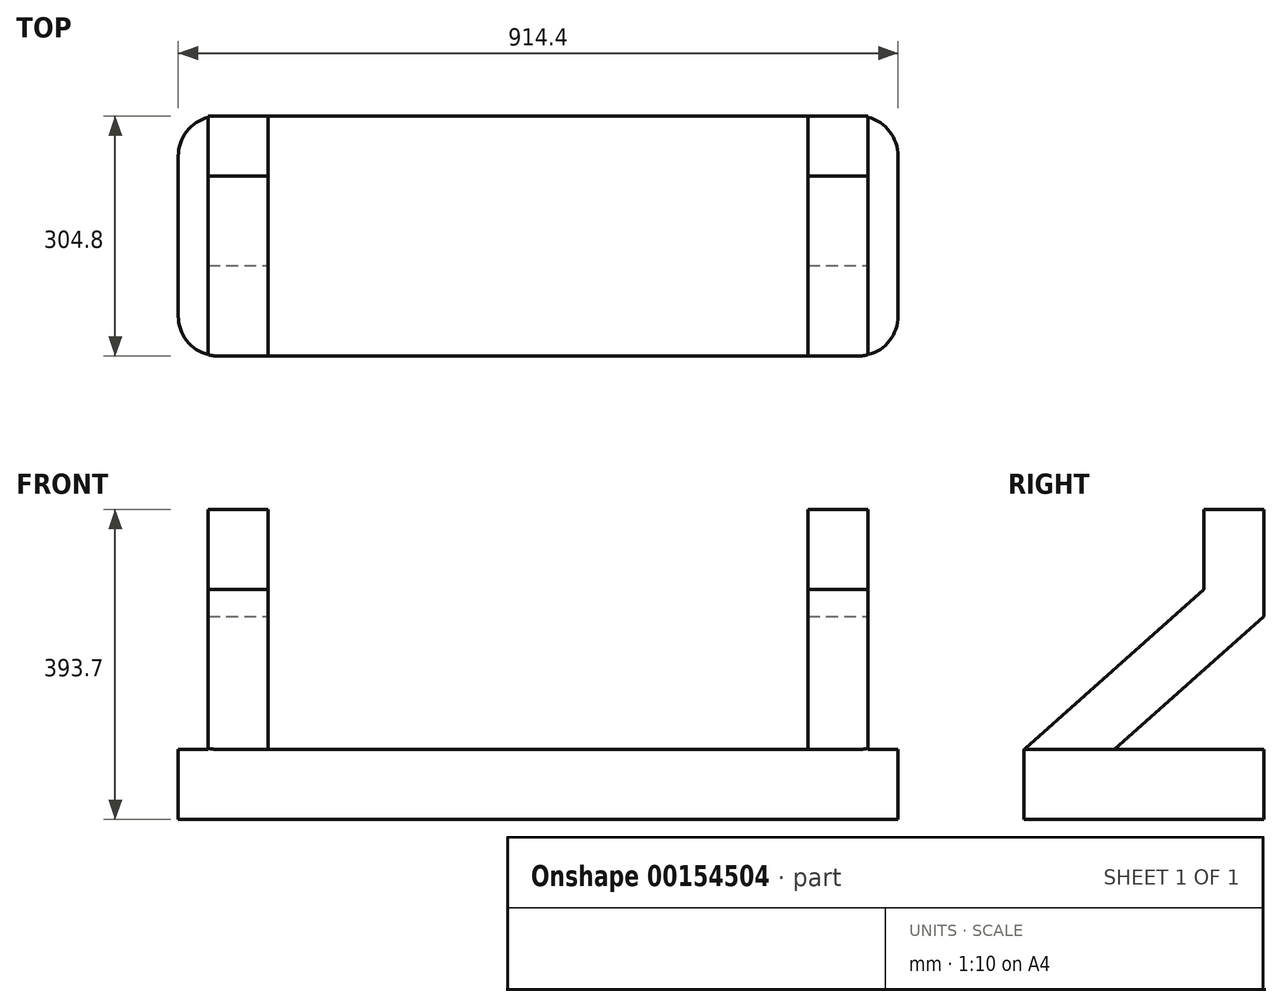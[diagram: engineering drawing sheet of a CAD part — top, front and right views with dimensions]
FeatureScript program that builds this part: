
annotation { "Feature Type Name" : "Feature", "Feature Type Description" : "" }
export const myFeature = defineFeature(function(context is Context, id is Id, definition is map)
    precondition{}
    {
        {
            var Q0;
            Q0=qCreatedBy(makeId("Top.planeOp"),FACE);
            var sketch = newSketch(context, id + "F0", { "sketchPlane" : qUnion([Q0])});
            skLineSegment(sketch, "E0.bottom", {"start": v(457.2, 152.4) * mm, "end": v(-457.2, 152.4) * mm});
            skLineSegment(sketch, "E0.top", {"start": v(457.2, -152.4) * mm, "end": v(-457.2, -152.4) * mm});
            skLineSegment(sketch, "E0.left", {"start": v(457.2, 152.4) * mm, "end": v(457.2, -152.4) * mm});
            skLineSegment(sketch, "E0.right", {"start": v(-457.2, 152.4) * mm, "end": v(-457.2, -152.4) * mm});
            skPoint(sketch, "E0.middle", {"position": v(0, 0) * mm});
            skSolve(sketch);
        }
        {
            var Q0;
            Q0=makeQuery(id+"F0.imprint","IMPRINT",FACE,{"disambiguationData":[TD([[makeQuery(id+"F0.imprint","IMPRINT",EDGE,{"derivedFrom":sQuery(id+"F0.wireOp",EDGE,"E0.bottom")}),1.0]])]});
            extrude(context, id + "F1", {"entities" : qUnion([Q0]), "depth" : 88.9 * mm});
        }
        {
            var Q0;
            Q0=makeQuery(id+"F1.opExtrude","CAP_FACE",FACE,{"disambiguationData":[OSD([sQuery(id+"F0.wireOp",EDGE,"E0.bottom"),sQuery(id+"F0.wireOp",EDGE,"E0.top"),sQuery(id+"F0.wireOp",EDGE,"E0.left"),sQuery(id+"F0.wireOp",EDGE,"E0.right")])],"isStart":false});
            var sketch = newSketch(context, id + "F2", { "sketchPlane" : qUnion([Q0])});
            skLineSegment(sketch, "E1.bottom", {"start": v(-419.1, 152.4) * mm, "end": v(-342.9, 152.4) * mm});
            skLineSegment(sketch, "E1.top", {"start": v(-419.1, -152.4) * mm, "end": v(-342.9, -152.4) * mm});
            skLineSegment(sketch, "E1.left", {"start": v(-419.1, 152.4) * mm, "end": v(-419.1, -152.4) * mm});
            skLineSegment(sketch, "E1.right", {"start": v(-342.9, 152.4) * mm, "end": v(-342.9, -152.4) * mm});
            skLineSegment(sketch, "E2.bottom", {"start": v(419.1, 152.4) * mm, "end": v(342.9, 152.4) * mm});
            skLineSegment(sketch, "E2.top", {"start": v(419.1, -152.4) * mm, "end": v(342.9, -152.4) * mm});
            skLineSegment(sketch, "E2.left", {"start": v(419.1, 152.4) * mm, "end": v(419.1, -152.4) * mm});
            skLineSegment(sketch, "E2.right", {"start": v(342.9, 152.4) * mm, "end": v(342.9, -152.4) * mm});
            skLineSegment(sketch, "E3", {"start": v(-342.9, 0) * mm, "end": v(342.9, 0) * mm, "construction": true});
            skLineSegment(sketch, "E4", {"start": v(-381, 152.4) * mm, "end": v(-381, -152.4) * mm, "construction": true});
            skLineSegment(sketch, "E5", {"start": v(381, 152.4) * mm, "end": v(381, -152.4) * mm, "construction": true});
            skSolve(sketch);
        }
        {
            var Q0;
            Q0=makeQuery(id+"F2.imprint","IMPRINT",FACE,{"disambiguationData":[TD([[makeQuery(id+"F2.imprint","IMPRINT",EDGE,{"derivedFrom":sQuery(id+"F2.wireOp",EDGE,"E1.bottom")}),1.0]])]});
            var Q1;
            Q1=makeQuery(id+"F2.imprint","IMPRINT",FACE,{"disambiguationData":[TD([[makeQuery(id+"F2.imprint","IMPRINT",EDGE,{"derivedFrom":sQuery(id+"F2.wireOp",EDGE,"E2.bottom")}),1.0]])]});
            extrude(context, id + "F3", {"entities" : qUnion([Q0, Q1]), "operationType" : NewBodyOperationType.ADD, "depth" : 304.8 * mm});
        }
        {
            var Q0;
            Q0=makeQuery(id+"F3.opExtrude","SWEPT_FACE",FACE,{"disambiguationData":[OSD([sQuery(id+"F2.wireOp",EDGE,"E2.left")])]});
            var sketch = newSketch(context, id + "F4", { "sketchPlane" : qUnion([Q0])});
            skLineSegment(sketch, "E6", {"start": v(76.2, 393.7) * mm, "end": v(76.2, 292.1) * mm});
            skLineSegment(sketch, "E7", {"start": v(76.2, 292.1) * mm, "end": v(-152.4, 88.9) * mm});
            skLineSegment(sketch, "E8", {"start": v(76.2, 393.7) * mm, "end": v(-152.4, 393.7) * mm});
            skLineSegment(sketch, "E9", {"start": v(-152.4, 393.7) * mm, "end": v(-152.4, 88.9) * mm});
            skLineSegment(sketch, "E10", {"start": v(152.4, 257.88) * mm, "end": v(-37.7, 88.9) * mm});
            skLineSegment(sketch, "E11", {"start": v(-37.7, 88.9) * mm, "end": v(152.4, 88.9) * mm});
            skLineSegment(sketch, "E12", {"start": v(152.4, 88.9) * mm, "end": v(152.4, 257.88) * mm});
            skSolve(sketch);
        }
        {
            var Q0;
            Q0=makeQuery(id+"F4.imprint","IMPRINT",FACE,{"disambiguationData":[TD([[makeQuery(id+"F4.imprint","IMPRINT",EDGE,{"derivedFrom":sQuery(id+"F4.wireOp",EDGE,"E6")}),-1.0]])]});
            var Q1;
            Q1=makeQuery(id+"F4.imprint","IMPRINT",FACE,{"disambiguationData":[TD([[makeQuery(id+"F4.imprint","IMPRINT",EDGE,{"derivedFrom":sQuery(id+"F4.wireOp",EDGE,"E10")}),1.0]])]});
            extrude(context, id + "F5", {"entities" : qUnion([Q0, Q1]), "operationType" : NewBodyOperationType.REMOVE, "endBound" : BoundingType.THROUGH_ALL, "oppositeDirection" : true, "depth" : 30.48 * mm});
        }
        {
            var Q0;
            Q0=makeQuery(id+"F1.opExtrude","SWEPT_EDGE",EDGE,{"disambiguationData":[OSD([sQuery(id+"F0.wireOp",EDGE,"E0.top"),sQuery(id+"F0.wireOp",EDGE,"E0.right")])]});
            var Q1;
            Q1=makeQuery(id+"F1.opExtrude","SWEPT_EDGE",EDGE,{"disambiguationData":[OSD([sQuery(id+"F0.wireOp",EDGE,"E0.top"),sQuery(id+"F0.wireOp",EDGE,"E0.left")])]});
            var Q2;
            Q2=makeQuery(id+"F1.opExtrude","SWEPT_EDGE",EDGE,{"disambiguationData":[OSD([sQuery(id+"F0.wireOp",EDGE,"E0.bottom"),sQuery(id+"F0.wireOp",EDGE,"E0.left")])]});
            var Q3;
            Q3=makeQuery(id+"F1.opExtrude","SWEPT_EDGE",EDGE,{"disambiguationData":[OSD([sQuery(id+"F0.wireOp",EDGE,"E0.bottom"),sQuery(id+"F0.wireOp",EDGE,"E0.right")])]});
            fillet(context, id + "F6", {"entities" : qUnion([Q0, Q1, Q2, Q3]), "radius" : 50.8 * mm, "tangentPropagation" : true, "allowEdgeOverflow" : false});
        }
    });
